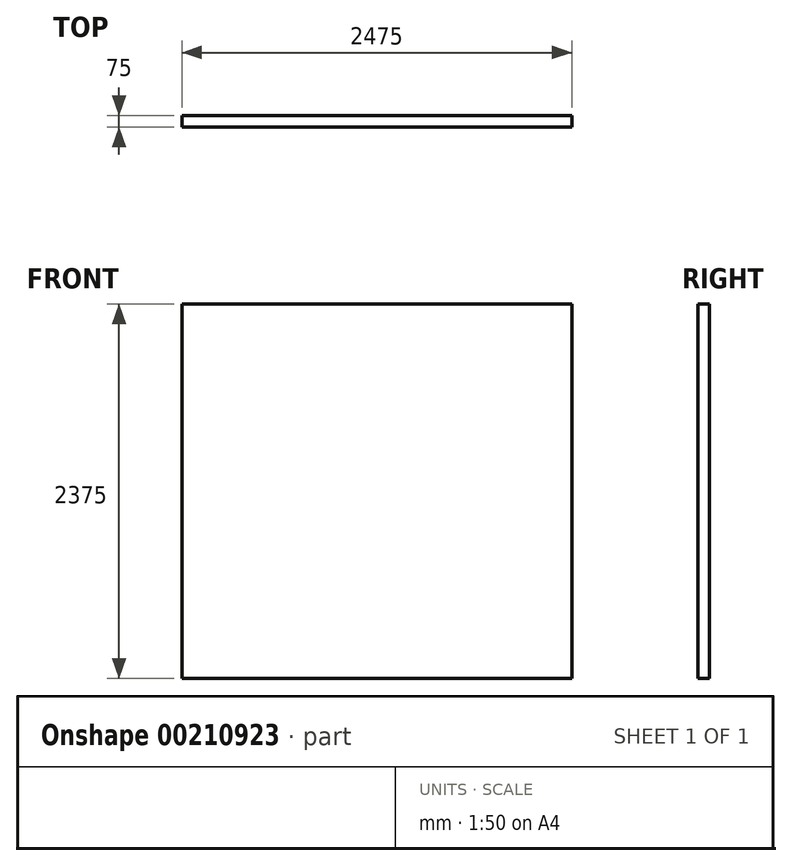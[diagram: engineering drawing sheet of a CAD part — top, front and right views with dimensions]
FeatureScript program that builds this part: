
annotation { "Feature Type Name" : "Feature", "Feature Type Description" : "" }
export const myFeature = defineFeature(function(context is Context, id is Id, definition is map)
    precondition{}
    {
        {
            var Q0;
            Q0=qCreatedBy(makeId("Front.planeOp"),FACE);
            var sketch = newSketch(context, id + "F0", { "sketchPlane" : qUnion([Q0])});
            skLineSegment(sketch, "E0.bottom", {"start": v(0, 0) * mm, "end": v(2475, 0) * mm});
            skLineSegment(sketch, "E0.right", {"start": v(2475, 0) * mm, "end": v(2475, 2375) * mm});
            skLineSegment(sketch, "E1", {"start": v(0, 2375) * mm, "end": v(2475, 2375) * mm});
            skLineSegment(sketch, "E2", {"start": v(0, 0) * mm, "end": v(0, 2375) * mm});
            skSolve(sketch);
        }
        {
            var Q0;
            Q0=makeQuery(id+"F0.imprint","IMPRINT",FACE,{"disambiguationData":[TD([[makeQuery(id+"F0.imprint","IMPRINT",EDGE,{"derivedFrom":sQuery(id+"F0.wireOp",EDGE,"E0.bottom")}),1.0]])]});
            extrude(context, id + "F1", {"entities" : qUnion([Q0]), "depth" : 75 * mm});
        }
    });
